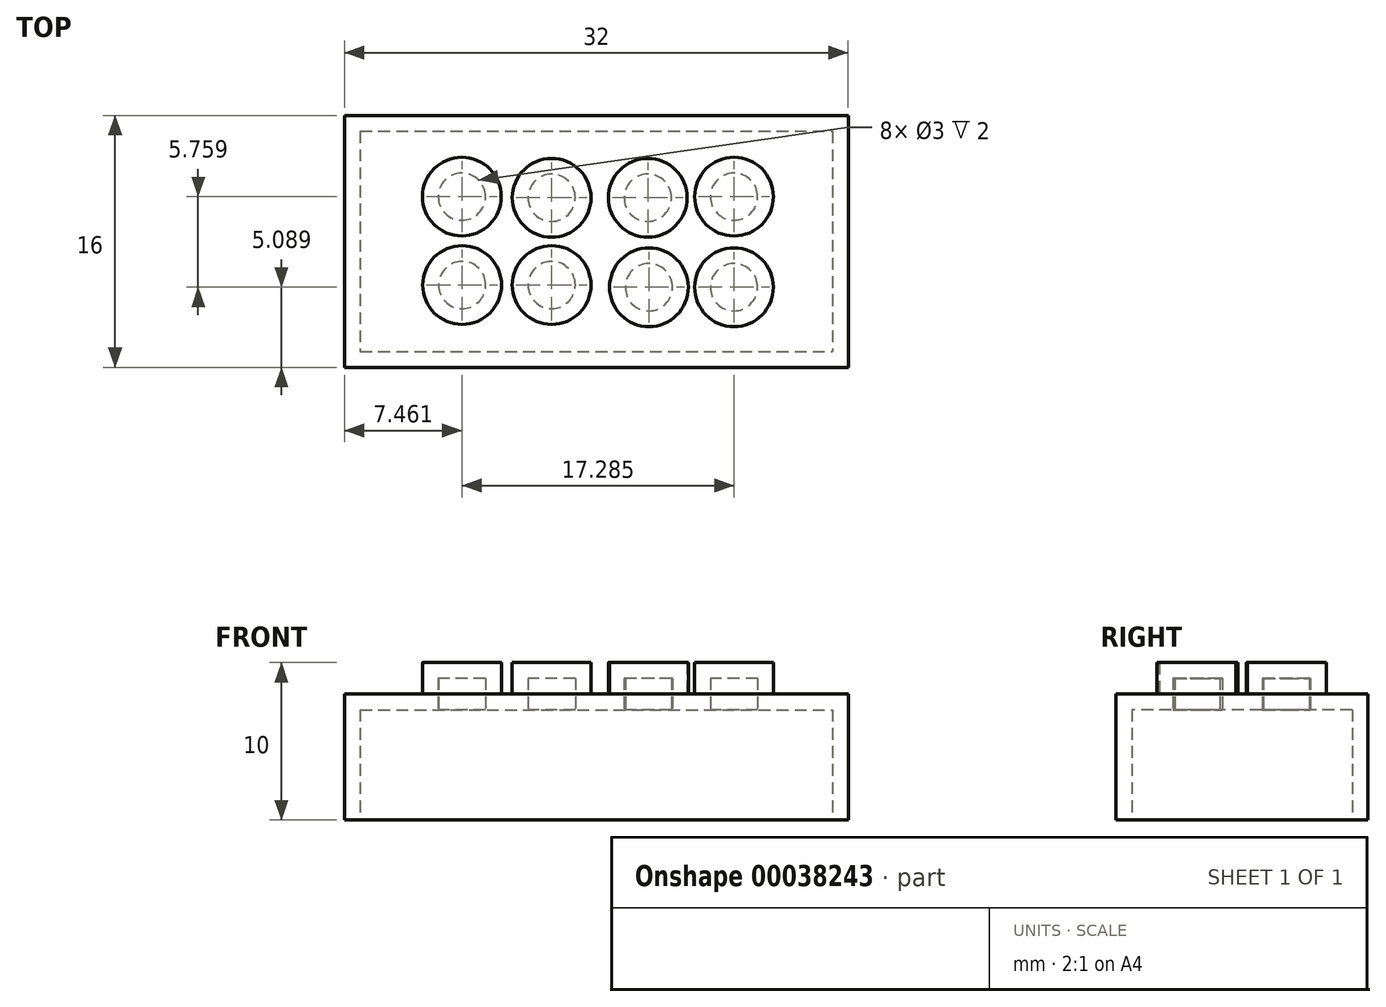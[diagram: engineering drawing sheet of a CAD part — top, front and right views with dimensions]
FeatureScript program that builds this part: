
annotation { "Feature Type Name" : "Feature", "Feature Type Description" : "" }
export const myFeature = defineFeature(function(context is Context, id is Id, definition is map)
    precondition{}
    {
        {
            var Q0;
            Q0=qCreatedBy(makeId("Top.planeOp"),FACE);
            var sketch = newSketch(context, id + "F0", { "sketchPlane" : qUnion([Q0])});
            skLineSegment(sketch, "E0.bottom", {"start": v(-15.93, 16) * mm, "end": v(16.07, 16) * mm});
            skLineSegment(sketch, "E0.top", {"start": v(-15.93, 0) * mm, "end": v(16.07, 0) * mm});
            skLineSegment(sketch, "E0.left", {"start": v(-15.93, 16) * mm, "end": v(-15.93, 0) * mm});
            skLineSegment(sketch, "E0.right", {"start": v(16.07, 16) * mm, "end": v(16.07, 0) * mm});
            skSolve(sketch);
        }
        {
            var Q0;
            Q0 = qSketchRegion(id + "F0", true);
            var Q1;
            Q1=makeQuery(id+"F0.imprint","IMPRINT",FACE,{"disambiguationData":[TD([[makeQuery(id+"F0.imprint","IMPRINT",EDGE,{"derivedFrom":sQuery(id+"F0.wireOp",EDGE,"E0.bottom")}),-1.0]])]});
            extrude(context, id + "F1", {"entities" : qUnion([Q0, Q1]), "depth" : 8 * mm});
        }
        {
            var Q0;
            Q0=qCreatedBy(makeId("Top.planeOp"),FACE);
            cPlane(context, id + "F2", {"entities" : qUnion([Q0]), "cplaneType" : CPlaneType.OFFSET, "offset" : 8 * mm, "width" : 150 * mm, "height" : 150 * mm});
        }
        {
            var Q0;
            Q0=qCreatedBy(id+"F2.planeOp",FACE);
            var sketch = newSketch(context, id + "F3", { "sketchPlane" : qUnion([Q0])});
            skLineSegment(sketch, "E1", {"start": v(-15.9, 10.85) * mm, "end": v(18.97, 10.85) * mm, "construction": true});
            skLineSegment(sketch, "E2", {"start": v(-15.78, 5.28) * mm, "end": v(19.21, 5.28) * mm, "construction": true});
            skLineSegment(sketch, "E3", {"start": v(-8.47, 18.04) * mm, "end": v(-8.47, -1.02) * mm, "construction": true});
            skLineSegment(sketch, "E4", {"start": v(-2.72, 18.16) * mm, "end": v(-2.72, -1.61) * mm, "construction": true});
            skLineSegment(sketch, "E5", {"start": v(3.4, 18.16) * mm, "end": v(3.4, -1.67) * mm, "construction": true});
            skLineSegment(sketch, "E6", {"start": v(8.9, 18.4) * mm, "end": v(8.9, -2.4) * mm, "construction": true});
            skCircle(sketch, "E7", {"center": v(-8.47, 10.85) * mm, "radius": 2.5 * mm});
            skCircle(sketch, "E8", {"center": v(-2.76, 10.77) * mm, "radius": 2.5 * mm});
            skCircle(sketch, "E9", {"center": v(3.34, 10.77) * mm, "radius": 2.5 * mm});
            skCircle(sketch, "E10", {"center": v(8.82, 10.84) * mm, "radius": 2.5 * mm});
            skCircle(sketch, "E11", {"center": v(-8.45, 5.23) * mm, "radius": 2.5 * mm});
            skCircle(sketch, "E12", {"center": v(-2.76, 5.23) * mm, "radius": 2.5 * mm});
            skCircle(sketch, "E13", {"center": v(3.41, 5.09) * mm, "radius": 2.5 * mm});
            skCircle(sketch, "E14", {"center": v(8.82, 5.09) * mm, "radius": 2.5 * mm});
            skSolve(sketch);
        }
        {
            var Q0;
            Q0=makeQuery(id+"F3.imprint","IMPRINT",FACE,{"disambiguationData":[TD([[makeQuery(id+"F3.imprint","IMPRINT",EDGE,{"derivedFrom":sQuery(id+"F3.wireOp",EDGE,"E7")}),1.0]])]});
            var Q1;
            Q1=makeQuery(id+"F3.imprint","IMPRINT",FACE,{"disambiguationData":[TD([[makeQuery(id+"F3.imprint","IMPRINT",EDGE,{"derivedFrom":sQuery(id+"F3.wireOp",EDGE,"E8")}),1.0]])]});
            var Q2;
            Q2=makeQuery(id+"F3.imprint","IMPRINT",FACE,{"disambiguationData":[TD([[makeQuery(id+"F3.imprint","IMPRINT",EDGE,{"derivedFrom":sQuery(id+"F3.wireOp",EDGE,"E9")}),1.0]])]});
            var Q3;
            Q3=makeQuery(id+"F3.imprint","IMPRINT",FACE,{"disambiguationData":[TD([[makeQuery(id+"F3.imprint","IMPRINT",EDGE,{"derivedFrom":sQuery(id+"F3.wireOp",EDGE,"E10")}),1.0]])]});
            var Q4;
            Q4=makeQuery(id+"F3.imprint","IMPRINT",FACE,{"disambiguationData":[TD([[makeQuery(id+"F3.imprint","IMPRINT",EDGE,{"derivedFrom":sQuery(id+"F3.wireOp",EDGE,"E14")}),1.0]])]});
            var Q5;
            Q5=makeQuery(id+"F3.imprint","IMPRINT",FACE,{"disambiguationData":[TD([[makeQuery(id+"F3.imprint","IMPRINT",EDGE,{"derivedFrom":sQuery(id+"F3.wireOp",EDGE,"E13")}),1.0]])]});
            var Q6;
            Q6=makeQuery(id+"F3.imprint","IMPRINT",FACE,{"disambiguationData":[TD([[makeQuery(id+"F3.imprint","IMPRINT",EDGE,{"derivedFrom":sQuery(id+"F3.wireOp",EDGE,"E12")}),1.0]])]});
            var Q7;
            Q7=makeQuery(id+"F3.imprint","IMPRINT",FACE,{"disambiguationData":[TD([[makeQuery(id+"F3.imprint","IMPRINT",EDGE,{"derivedFrom":sQuery(id+"F3.wireOp",EDGE,"E11")}),1.0]])]});
            extrude(context, id + "F4", {"entities" : qUnion([Q0, Q1, Q2, Q3, Q4, Q5, Q6, Q7]), "operationType" : NewBodyOperationType.ADD, "depth" : 2 * mm});
        }
        {
            var Q0;
            Q0=makeQuery(id+"F1.opExtrude","CAP_FACE",FACE,{"disambiguationData":[OSD([sQuery(id+"F0.wireOp",EDGE,"E0.bottom"),sQuery(id+"F0.wireOp",EDGE,"E0.top"),sQuery(id+"F0.wireOp",EDGE,"E0.left"),sQuery(id+"F0.wireOp",EDGE,"E0.right")])],"isStart":true});
            shell(context, id + "F5", {"entities" : qUnion([Q0]), "thickness" : 1 * mm});
        }
        {
            var Q0;
            Q0=makeQuery(id+"F0.imprint","IMPRINT",FACE,{"disambiguationData":[TD([[makeQuery(id+"F0.imprint","IMPRINT",EDGE,{"derivedFrom":sQuery(id+"F0.wireOp",EDGE,"E0.bottom")}),-1.0]])]});
            var sketch = newSketch(context, id + "F6", { "sketchPlane" : qUnion([Q0])});
            skCircle(sketch, "E15", {"center": v(-5.95, 7.7) * mm, "radius": 2.04 * mm});
            skCircle(sketch, "E16", {"center": v(0.31, 7.64) * mm, "radius": 2.04 * mm});
            skCircle(sketch, "E17", {"center": v(5.88, 7.48) * mm, "radius": 2.04 * mm});
            skSolve(sketch);
        }
        {
            var Q0;
            Q0=sQuery(id+"F6.wireOp",EDGE,"E15");
            var Q1;
            Q1=sQuery(id+"F6.wireOp",EDGE,"E16");
            var Q2;
            Q2=sQuery(id+"F6.wireOp",EDGE,"E17");
            extrude(context, id + "F7", {"bodyType" : ToolBodyType.SURFACE, "surfaceEntities" : qUnion([Q0, Q1, Q2]), "depth" : 2 * mm});
        }
    });
